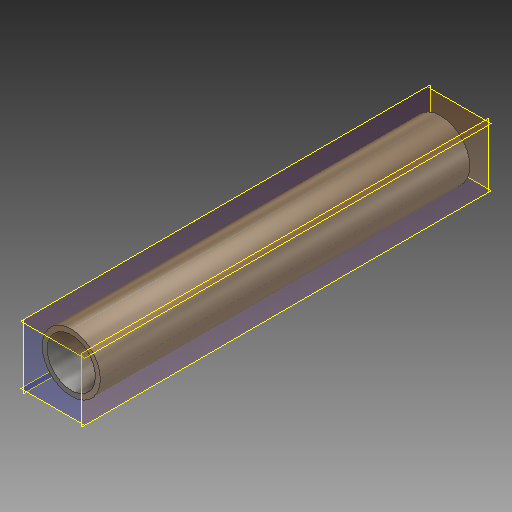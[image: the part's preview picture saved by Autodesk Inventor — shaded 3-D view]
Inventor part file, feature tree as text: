
AUTODESK INVENTOR PART (.ipt)
format: ipt  version: 2018 (Build 220112000, 112)  size: 117,248 bytes
history: native  units: mm
features: other x5, extrude x1, sketch x1
ambient origin geometry x8: Origin, YZ Plane, XZ Plane, XY Plane, X Axis, Y Axis, Z Axis, Center Point
bodies: Body1 (feature_tree)
feature tree (7):
  other  "ソリッド1"
  extrude  "押し出し1"  Depth=27.2mm
  other  "作業平面1"
  other  "作業平面3"
  other  "作業平面4"
  other  "作業平面5"
  sketch  "スケッチ1"
